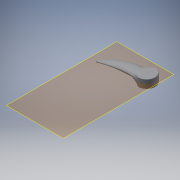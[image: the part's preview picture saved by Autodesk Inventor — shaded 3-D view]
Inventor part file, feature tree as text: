
AUTODESK INVENTOR PART (.ipt)
format: ipt  version: 2019 (Build 230136000, 136)  size: 370,176 bytes
history: native  units: mm
features: other x9, sketch x8, extrude x3, loft x2, fillet x2, revolve x1
ambient origin geometry x8: Origin, YZ Plane, XZ Plane, XY Plane, X Axis, Y Axis, Z Axis, Center Point
bodies: Body1 (feature_tree)
feature tree (25):
  other  "Твердое тело1"
  extrude  "Выдавливание1"  Depth=20.0mm TaperAngle=0.0deg
  other  "РабПлоскость5"
  loft  "Лофт3"
  other  "РабПлоскость6"
  sketch  "Эскиз11"
  revolve  "Вращение2"
  other  "РабПлоскость7"
  sketch  "Эскиз13"
  other  "РабПлоскость8"
  loft  "Лофт4"
  extrude  "Выдавливание3"  Depth=20.0mm
  extrude  "Выдавливание4"  TaperAngle=0.0deg  [1 undecoded]
  fillet  "Сопряжение2"  [1 undecoded]
  fillet  "Сопряжение3"  [1 undecoded]
  other  "РабПлоскость9"
  sketch  "Эскиз1"
  sketch  "Эскиз9"
  sketch  "Эскиз10"
  other  "Ребра4"
  sketch  "Эскиз12"
  sketch  "Эскиз14"
  other  "Ребра5"
  other  "Ребра6"
  sketch  "Эскиз15"
note: 3 required parameter values undecoded (feature->parameter linkage not recoverable at this tier; creation-order binding heuristic only, values carry confidence <= 0.55)
